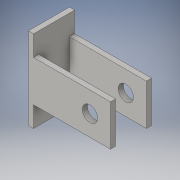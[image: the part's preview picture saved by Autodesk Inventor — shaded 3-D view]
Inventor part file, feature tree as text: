
AUTODESK INVENTOR PART (.ipt)
format: ipt  version: 2016 (Build 200138000, 138)  size: 126,464 bytes
history: native  units: in
note: dims shown in document units (in); Inventor stores cm internally (conversion verified against a paired STEP export)
features: extrude x4, sketch x4
ambient origin geometry x8: Origin, YZ Plane, XZ Plane, XY Plane, X Axis, Y Axis, Z Axis, Center Point
bodies: Solid1 (feature_tree)
feature tree (8):
  extrude  "Extrusion1"  Depth=0.125in
  extrude  "Extrusion2"  Depth=2.0in
  extrude  "Extrusion3"  Depth=0.5in TaperAngle=0.0deg
  extrude  "Extrusion4"  Depth=1.0in
  sketch  "Sketch1"  dims[d0=0.125in d1=0.125in]
  sketch  "Sketch2"  dims[d2=0.75in d3=2.0in]
  sketch  "Sketch3"  dims[d4=1.0in d5=0.0in d6=0.5in d7=0.0in]
  sketch  "Sketch4"  dims[d8=0.5in d9=0.0in d10=0.375in d11=0.5in d12=0.5in d13=1.0in d14=0.0in]
